# Revit family: Interior_Correr_Externa_c_Trilho_Metlico_de_2_Folhas_9160
name_source: partatom
category: Portas
revit_build: Autodesk Revit Architecture 2015 (Build: 20140606_1530(x64)
units: mm (PartAtom-declared; Revit-internal decimal feet)

## types (1)
- 1800 x 2100 mm
    Abertura = 0  [stored 0 ft]
    Abertura % = 0
    Aduela = Porta - Aduela Pintura de Cor Branco
    Aduela_Espessura = 15  [stored 0.0492126 ft]
    Altura = 2100
    Comentários de tipos = 100% Paramétrico
    Couceira = Porta - Couceira Pintura de Cor Branco
    Couceira_Lateral = 125  [stored 0.410105 ft]
    Couceira_Travessa Inferior = 165  [stored 0.541339 ft]
    Couceira_Travessa Superior = 125  [stored 0.410105 ft]
    Descrição = Porta de Madeira - Mógno c/ Vidro Liso
    Fabricante = CESARITA
    Fechamento da parede = Por hospedeiro
    Fecho_Pano Exterior = 15  [stored 0.0492126 ft]
    Função = Interior
    Grosseiro = Porta - Grosseiro Pintura de Cor Branco
    Guia = Metal - Aço Inox
    Largura = 1800  [stored 5.90551 ft]
    Modelo = 2 Folhas de Correr Externa
    Painel_Espessura = 40  [stored 0.131234 ft]
    Painel_Largura = 915  [stored 3.00197 ft]
    Puxador = Porta - Puxador
    Puxador_Altura = 550
    Puxador_Distância X = 63
    Puxador_Distância Y = 1070  [stored 3.5105 ft]
    Roldana = Metal - Aço Inox
    Roldana - Plástico = Plástico
    Roldana_Ressalto = 80  [stored 0.262467 ft]
    Trilho = Metal - Aço Inox
    Trilho_Afastado da Face da Parede = 13
    URL = www.cesarita.com
    Vidro = Porta - Vidro
    Vão_Altura = 2115
    Vão_Largura = 1830  [stored 6.00394 ft]

note: [stored X ft] marks values corroborated as IEEE doubles in the binary element streams (Revit-internal decimal feet)

## geometry (parser evidence)
native form markers: Blend x24, Sweep x9
no freeform markers — native parametric forms only
